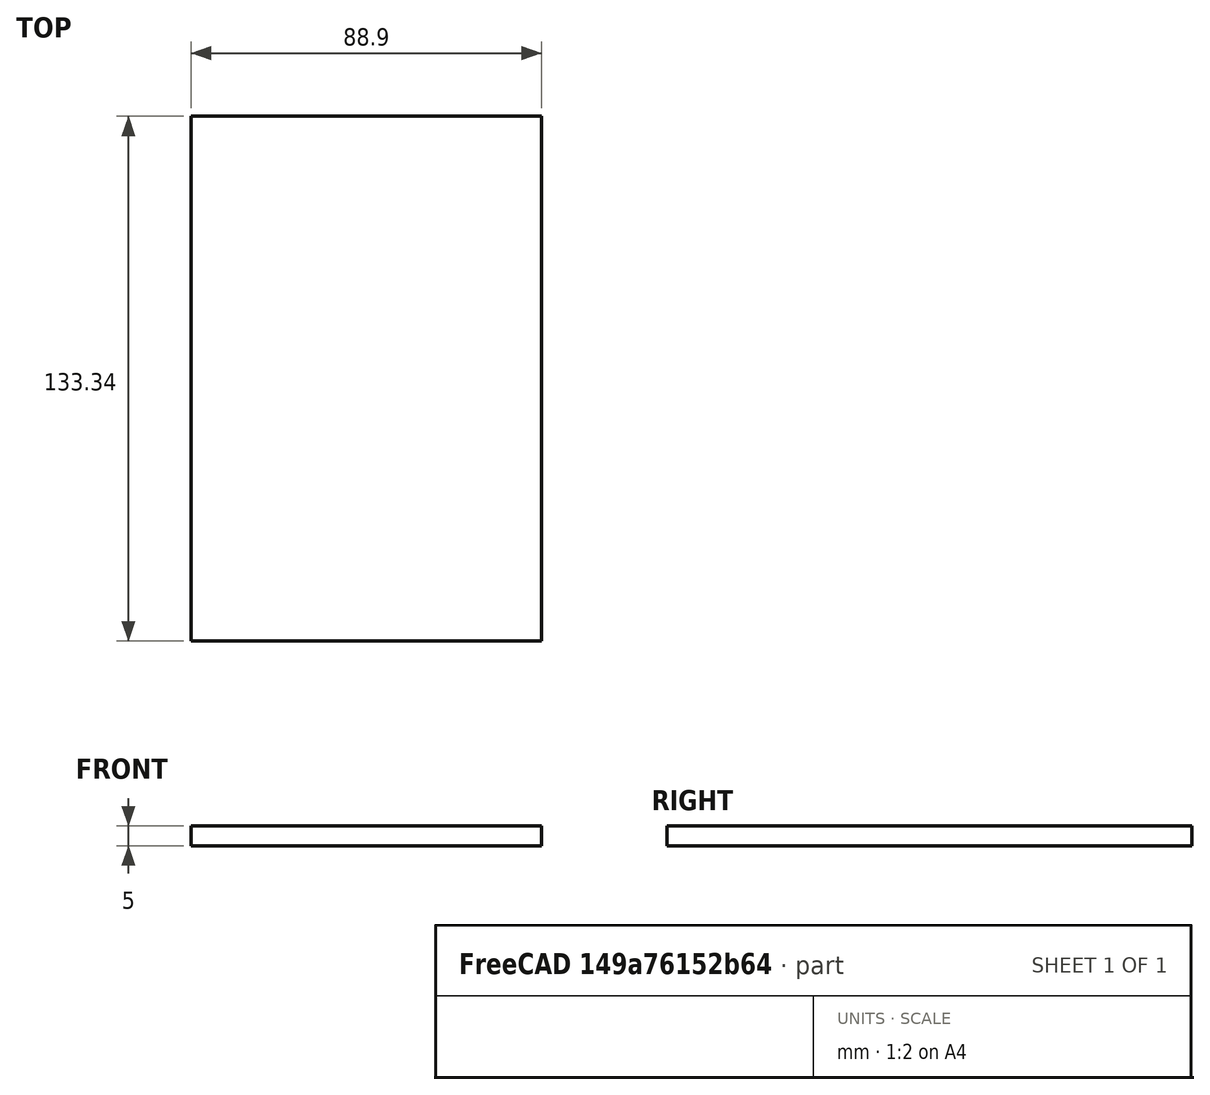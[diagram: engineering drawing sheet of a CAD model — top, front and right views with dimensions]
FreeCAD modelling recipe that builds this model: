
FCSTD DOCUMENT  (FreeCAD 0.16R)
Label: Plate
License: All rights reserved
LicenseURL: http://en.wikipedia.org/wiki/All_rights_reserved
objects: Sketcher::SketchObject×2, PartDesign::Pad×1, Spreadsheet::Sheet×1
note: 4 computed .brp shape members not serialized (recipe doc carries the construction recipe); baked Part::Feature solids carry a one-line shape summary decoded from their .brp

FEATURE [Sketcher::SketchObject] Sketch
  expr: Constraints[10] = Sketch.Constraints.PlateWidth / 2
  expr: Constraints[11] = Sketch.Constraints.PlateHeight / 2
  sketch-geometry (4):
    g0: LineSegment StartX=-44.45 StartY=-66.675 StartZ=0 EndX=44.45 EndY=-66.675 EndZ=0
    g1: LineSegment StartX=44.45 StartY=-66.675 StartZ=0 EndX=44.45 EndY=66.675 EndZ=0
    g2: LineSegment StartX=44.45 StartY=66.675 StartZ=0 EndX=-44.45 EndY=66.675 EndZ=0
    g3: LineSegment StartX=-44.45 StartY=66.675 StartZ=0 EndX=-44.45 EndY=-66.675 EndZ=0
  constraints (12):
    c: Coincident(g0,g1)
    c: Coincident(g1,g2)
    c: Coincident(g2,g3)
    c: Coincident(g3,g0)
    c: Horizontal(g0)
    c: Horizontal(g2)
    c: Vertical(g1)
    c: Vertical(g3)
    c: Distance(g2) = 88.9  'PlateWidth'
    c: Distance(g3) = 133.35  'PlateHeight'
    c: DistanceX(g-1,g0) = 44.45
    c: DistanceY(g0,g-1) = 66.675
FEATURE [PartDesign::Pad] Pad
  Length = 5
  Length2 = 100
  Sketch = -> Sketch
  Type = 0
FEATURE [Sketcher::SketchObject] Sketch001
  Placement = pos=(0,0,5) rot=(0,0,1;0rad)
  Support = -> Pad [Face6]
  expr: Constraints[10] = Sketch001.Constraints.ScreenWidth / 2
  expr: Constraints[11] = Sketch001.Constraints.ScreenHeight / 2
  sketch-geometry (4):
    g0: LineSegment StartX=-25 StartY=-35 StartZ=0 EndX=25 EndY=-35 EndZ=0
    g1: LineSegment StartX=25 StartY=-35 StartZ=0 EndX=25 EndY=35 EndZ=0
    g2: LineSegment StartX=25 StartY=35 StartZ=0 EndX=-25 EndY=35 EndZ=0
    g3: LineSegment StartX=-25 StartY=35 StartZ=0 EndX=-25 EndY=-35 EndZ=0
  constraints (12):
    c: Coincident(g0,g1)
    c: Coincident(g1,g2)
    c: Coincident(g2,g3)
    c: Coincident(g3,g0)
    c: Horizontal(g0)
    c: Horizontal(g2)
    c: Vertical(g1)
    c: Vertical(g3)
    c: Distance(g2) = 50  'ScreenWidth'
    c: Distance(g1) = 70  'ScreenHeight'
    c: DistanceX(g-1,g0) = 25
    c: DistanceY(g0,g-1) = 35
FEATURE [Spreadsheet::Sheet] Spreadsheet
